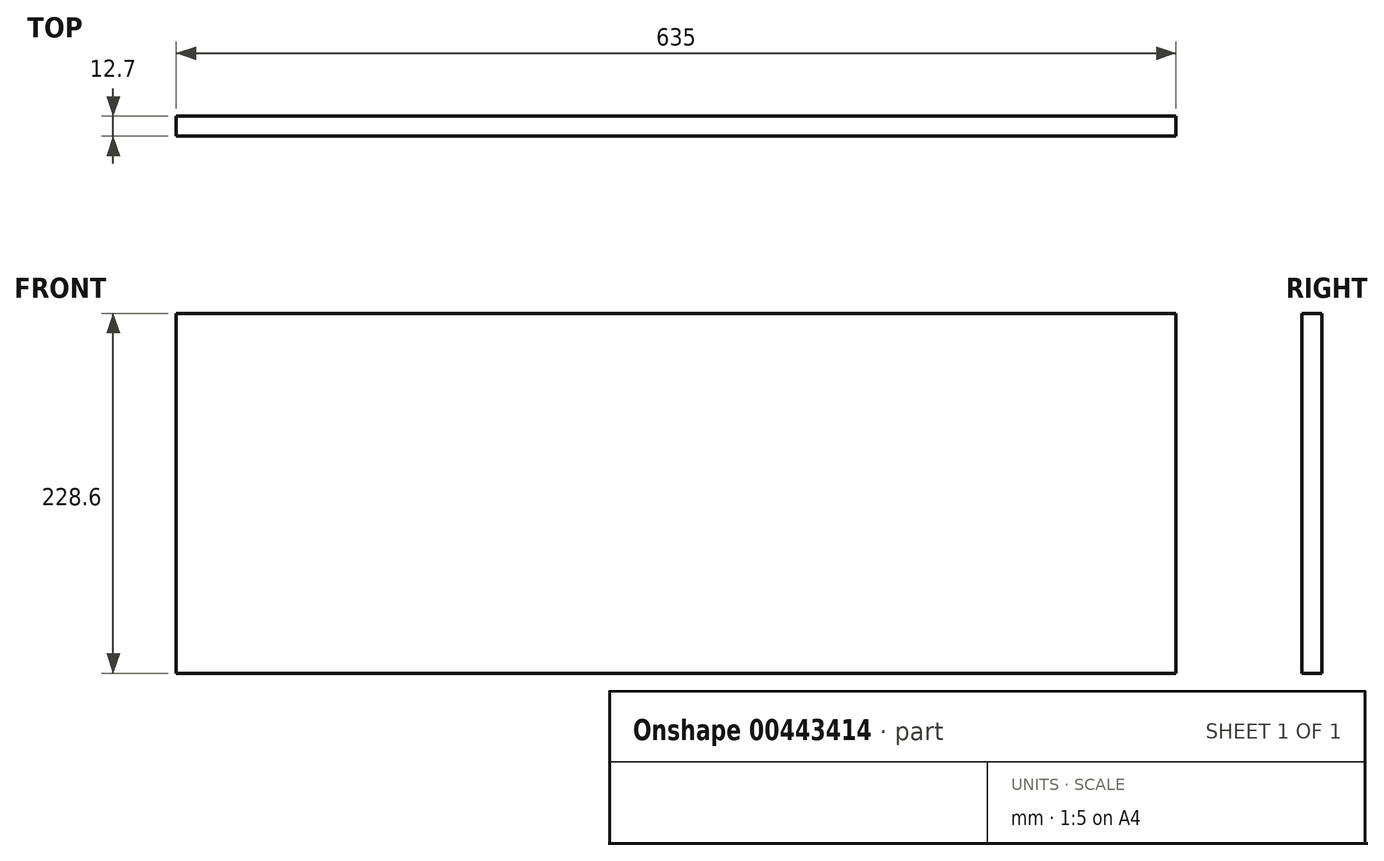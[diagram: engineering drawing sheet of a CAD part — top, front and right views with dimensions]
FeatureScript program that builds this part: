
annotation { "Feature Type Name" : "Feature", "Feature Type Description" : "" }
export const myFeature = defineFeature(function(context is Context, id is Id, definition is map)
    precondition{}
    {
        {
            var Q0;
            Q0=qCreatedBy(makeId("Front.planeOp"),FACE);
            var sketch = newSketch(context, id + "F0", { "sketchPlane" : qUnion([Q0])});
            skLineSegment(sketch, "E0.bottom", {"start": v(-317.5, 114.3) * mm, "end": v(317.5, 114.3) * mm});
            skLineSegment(sketch, "E0.top", {"start": v(-317.5, -114.3) * mm, "end": v(317.5, -114.3) * mm});
            skLineSegment(sketch, "E0.left", {"start": v(-317.5, 114.3) * mm, "end": v(-317.5, -114.3) * mm});
            skLineSegment(sketch, "E0.right", {"start": v(317.5, 114.3) * mm, "end": v(317.5, -114.3) * mm});
            skPoint(sketch, "E0.middle", {"position": v(0, 0) * mm});
            skSolve(sketch);
        }
        {
            var Q0;
            Q0 = qSketchRegion(id + "F0", true);
            extrude(context, id + "F1", {"entities" : qUnion([Q0]), "depth" : 12.7 * mm});
        }
    });
